# Revit family: BIMLIB_Конвектор_ВстраиваемыйВПолСЕстественнойКонвекцией_ВК200_VITRON
name_source: partatom
category: Оборудование
revit_build: Autodesk Revit 2017 (Build: 20190508_0315(x64)
units: mm (PartAtom-declared; Revit-internal decimal feet)

## family parameters
Всегда вертикально = Да
На основе рабочей плоскости = Нет
Общий = Нет
При загрузке вырезать с полостями = Нет
Размер круглого соединителя = Использовать диаметр
Тип детали = Нормальный
Точка расчета площади = Нет

## types (2) — shared parameters
ADSK_URL документации изделия = https://vitron.ru
ADSK_URL страницы изделия = https://vitron.ru
ADSK_Версия Revit = 2017
ADSK_Единица измерения = шт.
ADSK_Завод-изготовитель = Вилма / VITRON
ADSK_Размер_Высота = 200 мм
ADSK_Размер_Диаметр = 15 мм
BL_BIM library = https://bimlib.pro
URL = https://vitron.ru
VIT_Максимальная рабочая температура теплоносителя = 95 °C
VIT_Рабочее давление теплоносителя = 1600000.0 Па
Высота теплообменника = 100 мм
Изготовитель = Вилма / VITRON
Материал_Корпуса = BIMLIB_ОцинкованнаяСталь_VITRON
Материал_Решетка = BIMLIB_Алюминий_VITRON
Описание = Встраиваемый в пол конвектор с естественной конвекцией VITRON - отопительный прибор, в котором установлен медно-алюминиевый теплообменник, тепло от которого передаётся в отапливаемое помещение путём естественной конвекции. Позволяет преградить поток холодного воздуха от застеклённых фасадов или окон. Данный тип конвектора служит для отопления только сухих помещений. Применяется в качестве основного отопительного прибора в помещениях с небольшими потребностями в отоплении или вспомогательного отопительного прибора с системами тёплого пола, вентиляции, радиаторного водяного отопления. Может быть установлен как в однотрубную, так и в двухтрубную систему отопления.
Подключение с торца = Подключение с торца
Подключение сверху = Подключение сверху
Подключение снизу = Подключение снизу

## per-type parameters (varying)
| type | ADSK_Обозначение | ADSK_Размер_Ширина | VIT_Тепловая мощность на 1 м | Количество труб теплообменника | Коэффициент n | Расстояние между патрубками | Ширина теплообменника |
| Конвектор_Шириной 260мм | ВК.200.260 | 260 мм | 1038.848 Вт | 4 | 1.3 | 50 мм | 100 мм |
| Конвектор_Шириной 360мм | ВК.200.360 | 360 мм | 1874.317 Вт | 8 | 1.26 | 150 мм | 200 мм |
